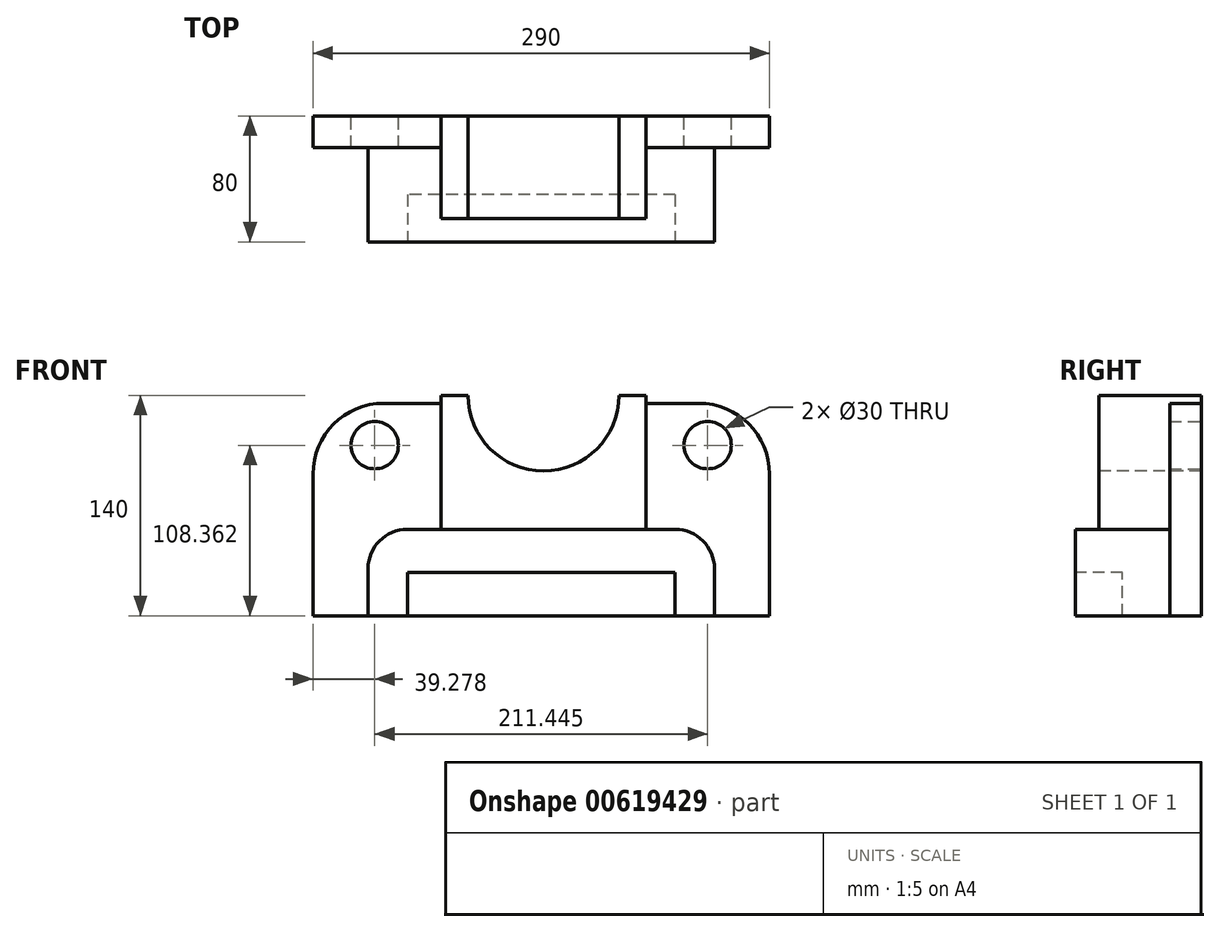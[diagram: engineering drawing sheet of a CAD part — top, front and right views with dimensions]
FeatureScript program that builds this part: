
annotation { "Feature Type Name" : "Feature", "Feature Type Description" : "" }
export const myFeature = defineFeature(function(context is Context, id is Id, definition is map)
    precondition{}
    {
        {
            var Q0;
            Q0=qCreatedBy(makeId("Front.planeOp"),FACE);
            var sketch = newSketch(context, id + "F0", { "sketchPlane" : qUnion([Q0])});
            skLineSegment(sketch, "E0.bottom", {"start": v(85, 27.5) * mm, "end": v(-85, 27.5) * mm});
            skLineSegment(sketch, "E0.top", {"start": v(110, -27.5) * mm, "end": v(-110, -27.5) * mm});
            skLineSegment(sketch, "E0.left", {"start": v(110, 2.5) * mm, "end": v(110, -27.5) * mm});
            skLineSegment(sketch, "E0.right", {"start": v(-110, 2.5) * mm, "end": v(-110, -27.5) * mm});
            skPoint(sketch, "E0.middle", {"position": v(0, 0) * mm});
            skPoint(sketch, "E1.visualSharp", {"position": v(-110, 27.5) * mm});
            skArc(sketch, "E1.filletArc", {"start": v(-85, 27.5) * mm, "mid": v(-102.68, 20.18) * mm, "end": v(-110, 2.5) * mm});
            skPoint(sketch, "E2.visualSharp", {"position": v(110, 27.5) * mm});
            skArc(sketch, "E2.filletArc", {"start": v(110, 2.5) * mm, "mid": v(102.68, 20.18) * mm, "end": v(85, 27.5) * mm});
            skSolve(sketch);
        }
        {
            var Q0;
            Q0 = qSketchRegion(id + "F0", true);
            extrude(context, id + "F1", {"entities" : qUnion([Q0]), "depth" : 80 * mm, "offsetDistance" : 25 * mm});
        }
        {
            var Q0;
            Q0=makeQuery(id+"F1.opExtrude","CAP_FACE",FACE,{"disambiguationData":[OSD([sQuery(id+"F0.wireOp",EDGE,"E0.bottom"),sQuery(id+"F0.wireOp",EDGE,"E0.top"),sQuery(id+"F0.wireOp",EDGE,"E0.left"),sQuery(id+"F0.wireOp",EDGE,"E0.right"),sQuery(id+"F0.wireOp",EDGE,"E1.filletArc"),sQuery(id+"F0.wireOp",EDGE,"E2.filletArc")])],"isStart":false});
            var sketch = newSketch(context, id + "F2", { "sketchPlane" : qUnion([Q0])});
            skLineSegment(sketch, "E3", {"start": v(-85, -27.5) * mm, "end": v(-85, 0) * mm});
            skLineSegment(sketch, "E4", {"start": v(-85, 0) * mm, "end": v(85, 0) * mm});
            skLineSegment(sketch, "E5", {"start": v(85, 0) * mm, "end": v(85, -27.5) * mm});
            skSolve(sketch);
        }
        {
            var Q0;
            {var subQ0=sQuery(id+"F2.wireOp",EDGE,"E3");Q0=makeQuery(id+"F2.imprint","IMPRINT",FACE,{"disambiguationData":[TD([[makeQuery(id+"F2.imprint","IMPRINT",EDGE,{"derivedFrom":subQ0}),-1.0]])]});}
            extrude(context, id + "F3", {"entities" : qUnion([Q0]), "operationType" : NewBodyOperationType.REMOVE, "oppositeDirection" : true, "depth" : 30 * mm, "offsetDistance" : 25 * mm});
        }
        {
            var Q0;
            Q0=makeQuery(id+"F1.opExtrude","CAP_FACE",FACE,{"disambiguationData":[OSD([sQuery(id+"F0.wireOp",EDGE,"E0.bottom"),sQuery(id+"F0.wireOp",EDGE,"E0.top"),sQuery(id+"F0.wireOp",EDGE,"E0.left"),sQuery(id+"F0.wireOp",EDGE,"E0.right"),sQuery(id+"F0.wireOp",EDGE,"E1.filletArc"),sQuery(id+"F0.wireOp",EDGE,"E2.filletArc")])],"isStart":false});
            cPlane(context, id + "F4", {"entities" : qUnion([Q0]), "cplaneType" : CPlaneType.OFFSET, "offset" : 15 * mm, "oppositeDirection" : true, "width" : 150 * mm, "height" : 150 * mm});
        }
        {
            var Q0;
            Q0=qCreatedBy(id+"F4.planeOp",FACE);
            var sketch = newSketch(context, id + "F5", { "sketchPlane" : qUnion([Q0])});
            skLineSegment(sketch, "E6", {"start": v(-63.56, 112.5) * mm, "end": v(-63.56, 27.5) * mm});
            skLineSegment(sketch, "E7", {"start": v(-63.56, 27.5) * mm, "end": v(66.44, 27.5) * mm});
            skLineSegment(sketch, "E8", {"start": v(66.44, 27.5) * mm, "end": v(66.44, 112.5) * mm});
            skLineSegment(sketch, "E9", {"start": v(66.44, 112.5) * mm, "end": v(49.44, 112.5) * mm});
            skPoint(sketch, "E10.startSnap0", {"position": v(1.44, 112.5) * mm});
            skLineSegment(sketch, "E11", {"start": v(-63.56, 112.5) * mm, "end": v(-46.56, 112.5) * mm});
            skLineSegment(sketch, "E12.trimOffspring", {"start": v(-46.56, 112.5) * mm, "end": v(-63.56, 112.5) * mm});
            skLineSegment(sketch, "E13", {"start": v(1.44, 27.5) * mm, "end": v(1.44, 163.16) * mm, "construction": true});
            skLineSegment(sketch, "E14", {"start": v(-63.56, 70) * mm, "end": v(66.44, 70) * mm, "construction": true});
            skCircle(sketch, "E15", {"center": v(1.44, 112.5) * mm, "radius": 48 * mm});
            skSolve(sketch);
        }
        {
            var Q0;
            Q0=makeQuery(id+"F5.imprint","IMPRINT",FACE,{"disambiguationData":[TD([[makeQuery(id+"F5.imprint","IMPRINT",EDGE,{"derivedFrom":sQuery(id+"F5.wireOp",EDGE,"E6")}),1.0]])]});
            extrude(context, id + "F6", {"entities" : qUnion([Q0]), "operationType" : NewBodyOperationType.ADD, "oppositeDirection" : true, "depth" : 65 * mm, "offsetDistance" : 25 * mm});
        }
        {
            var Q0;
            Q0=makeQuery(id+"F1.opExtrude","CAP_FACE",FACE,{"disambiguationData":[OSD([sQuery(id+"F0.wireOp",EDGE,"E0.bottom"),sQuery(id+"F0.wireOp",EDGE,"E0.top"),sQuery(id+"F0.wireOp",EDGE,"E0.left"),sQuery(id+"F0.wireOp",EDGE,"E0.right"),sQuery(id+"F0.wireOp",EDGE,"E1.filletArc"),sQuery(id+"F0.wireOp",EDGE,"E2.filletArc")])],"isStart":false});
            cPlane(context, id + "F7", {"entities" : qUnion([Q0]), "cplaneType" : CPlaneType.OFFSET, "offset" : 80 * mm, "oppositeDirection" : true, "width" : 150 * mm, "height" : 150 * mm});
        }
        {
            var Q0;
            Q0=qCreatedBy(id+"F7.planeOp",FACE);
            var sketch = newSketch(context, id + "F8", { "sketchPlane" : qUnion([Q0])});
            skLineSegment(sketch, "E16", {"start": v(0, 124.4) * mm, "end": v(0, -50.97) * mm, "construction": true});
            skLineSegment(sketch, "E17", {"start": v(66.44, 107.5) * mm, "end": v(100, 107.5) * mm});
            skLineSegment(sketch, "E18", {"start": v(145, 62.5) * mm, "end": v(145, -27.5) * mm});
            skLineSegment(sketch, "E19", {"start": v(145, -27.5) * mm, "end": v(110, -27.5) * mm});
            skCircle(sketch, "E20", {"center": v(105.72, 80.86) * mm, "radius": 15 * mm});
            skPoint(sketch, "E20.centerSnap0", {"position": v(105.72, 107.5) * mm});
            skPoint(sketch, "E21.visualSharp", {"position": v(145, 107.5) * mm});
            skArc(sketch, "E21.filletArc", {"start": v(145, 62.5) * mm, "mid": v(131.82, 94.32) * mm, "end": v(100, 107.5) * mm});
            skArc(sketch, "E22.MirrorCS", {"start": v(-145, 62.5) * mm, "mid": v(-131.82, 94.32) * mm, "end": v(-100, 107.5) * mm});
            skLineSegment(sketch, "E23.MirrorCS", {"start": v(-145, 62.5) * mm, "end": v(-145, -27.5) * mm});
            skLineSegment(sketch, "E24.MirrorCS", {"start": v(-145, -27.5) * mm, "end": v(-110, -27.5) * mm});
            skCircle(sketch, "E25.MirrorC", {"center": v(-105.72, 80.86) * mm, "radius": 15 * mm});
            skLineSegment(sketch, "E26", {"start": v(-100, 107.5) * mm, "end": v(-63.56, 107.5) * mm});
            skLineSegment(sketch, "E27", {"start": v(-63.56, 107.5) * mm, "end": v(-63.56, 27.5) * mm});
            skLineSegment(sketch, "E28", {"start": v(-63.56, 27.5) * mm, "end": v(-85, 27.5) * mm});
            skLineSegment(sketch, "E29", {"start": v(-110, 2.5) * mm, "end": v(-110, -27.5) * mm});
            skPoint(sketch, "E30.visualSharp", {"position": v(-110, 27.5) * mm});
            skArc(sketch, "E30.filletArc", {"start": v(-85, 27.5) * mm, "mid": v(-102.68, 20.18) * mm, "end": v(-110, 2.5) * mm});
            skLineSegment(sketch, "E31", {"start": v(66.44, 107.5) * mm, "end": v(66.44, 27.5) * mm});
            skLineSegment(sketch, "E32", {"start": v(110, -27.5) * mm, "end": v(110, 2.5) * mm});
            skLineSegment(sketch, "E33", {"start": v(85, 27.5) * mm, "end": v(66.44, 27.5) * mm});
            skPoint(sketch, "E34.visualSharp", {"position": v(110, 27.5) * mm});
            skArc(sketch, "E34.filletArc", {"start": v(110, 2.5) * mm, "mid": v(102.68, 20.18) * mm, "end": v(85, 27.5) * mm});
            skSolve(sketch);
        }
        {
            var Q0;
            Q0 = qSketchRegion(id + "F8", true);
            extrude(context, id + "F9", {"entities" : qUnion([Q0]), "operationType" : NewBodyOperationType.ADD, "depth" : 20 * mm, "offsetDistance" : 25 * mm});
        }
    });
